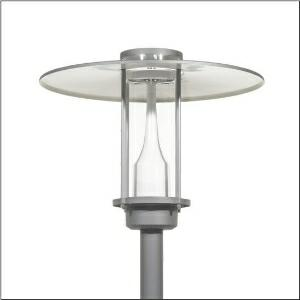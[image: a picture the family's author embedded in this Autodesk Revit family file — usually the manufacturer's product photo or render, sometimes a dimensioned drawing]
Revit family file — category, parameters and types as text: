
# Revit family: city-light_plus_iq___pl1_2s_5xa5275of14h_1ed9
name_source: partatom
category: Lighting Fixtures
units: mm (PartAtom-declared; Revit-internal decimal feet)

## family parameters
Cut with Voids When Loaded = No
Host = Face
Light Source = No
Part Type = Normal
Room Calculation Point = No
Round Connector Dimension = Use Diameter
Shared = No

## types (1)
- --- (1 x LED, 2840 lm, 21.8 W, 2700K)
    Apparent Load = 22 VA
    CIE Flux Codes = 23 63 93 97 100
    Color Rendering = 70
    Color Temperature = 2700K
    Default Elevation = 1800 mm
    Description = City-Light Plus iQ, mast luminaire, Module 540 iQ-SR, primary light control with 3 zone facetted reflector, of plastic, silver coated, highly specular, structured, primary optical cover: cover, of PMMA, transparent, light distribution: PL1.2s, light emission: direct distribution, primary light characteristic: symmetric, installation type: post-top, LED, High Power LED, rated luminous flux: 2.840lm, luminous efficacy: 130lm/W, light colour: 727, colour temperature: 2700K, control gear: iQ Street-Remote, control: pre-setting: logarithmic dimming characteristic, Street-Remote, Auto-Match, Temp-Guard, Lumen-Switch, Night-Set, Smart-Wire, Light-Fading, Desk-Remote (wireless, voltage-free reading and setting of iQ features in the workshop via application-optimized NFC function/RFID function), optimised constant luminous flux control (CLO 2.0), with terminal, 6-pole, max. 2.5mm², mains connection: 230..240V, AC, 50/60Hz, start of lifetime: 22W, end of service life: 23W, reduction: 11W, luminaire housing, upper part, of glass-fibre reinforced polyester, coated, Siteco® metallic grey (DB 702S), diameter: 750mm, height: 590mm, spigot size: d x l = 76 x 70mm (post-top) | with reducer (optional accessory) 60 x 70mm, mounting height: 3..5m, post-top mast mounting element, of diecast aluminium, coated, Siteco® metallic grey (DB 702S), Module 540 iQ-SR, traffic white (RAL 9016), equipment: standard, protection rating (complete): IP65, insulation class (complete): insulation class II (safety insulation), certification: CE, ENEC, VDE, packaging unit: 1 piece

Light Distribution: PL1.2s
    Height = 590 mm
    Lamp = 1 x LED
    Lamp Light Flux = 2840 lm
    Lamp Power = 21.8 W
    Lamp count = 1
    Length = 750 mm
    Luminous efficacy = 130 lm/W
    Manufacturer = Siteco
    ModVariant = No
    Model = 5XA5275OF14H
    Number of Poles = 1
    OnlyDefault = Yes
    Power Factor = 1
    Product Name = City-Light Plus iQ | PL1.2s
    Product group = mast luminaire | pylon top
    ProductGroupID = 6100
    Protection Class = Protection class II
    Protection Degree = IP 65
    RLX_Detail_Level = 1
    RLX_Emergency_Light_Flux = 0 lm
    RLX_Emergency_Type = 0
    RLX_Emergency_Type_DB = No
    RlxData = <blob elided: 33141 chars, md5=7d06be9b>
    Socket = socket
    Standby Power = 0 W
    System Light Flux = 2840 lm
    System Power = 22 W
    Type Comments = factory setting: luminous flux: 100 % | dim-lin: 254 | 456 mA
    Type Image = l_1006456.jpg
    URL = http://relux.com
    VarID = @adj_145450
    Voltage = 0 V
    Weight = 0.00 kg
    Width = 0 mm  [stored 0 ft]

note: [stored X ft] marks values corroborated as IEEE doubles in the binary element streams (Revit-internal decimal feet)

## geometry (parser evidence)
native form markers: Blend x4, Sweep x9
no freeform markers — native parametric forms only
